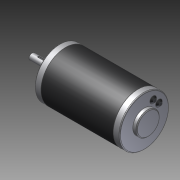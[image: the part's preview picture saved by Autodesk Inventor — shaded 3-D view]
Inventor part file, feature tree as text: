
AUTODESK INVENTOR PART (.ipt)
format: ipt  version: 2014 SP1 (Build 180222100, 222)  size: 151,552 bytes
history: native  units: in
note: dims shown in document units (in); Inventor stores cm internally (conversion verified against a paired STEP export)
features: chamfer x1, other x1, imported_body x1
ambient origin geometry x8: Origin, YZ Plane, XZ Plane, XY Plane, X Axis, Y Axis, Z Axis, Center Point
bodies: Body1 (feature_tree)
feature tree (3):
  chamfer  "Chamfer3"  [1 undecoded]
  other  "217-2000.ipt1"
  imported_body  "Base1"
note: 1 required parameter value undecoded (feature->parameter linkage not recoverable at this tier; creation-order binding heuristic only, values carry confidence <= 0.55)
